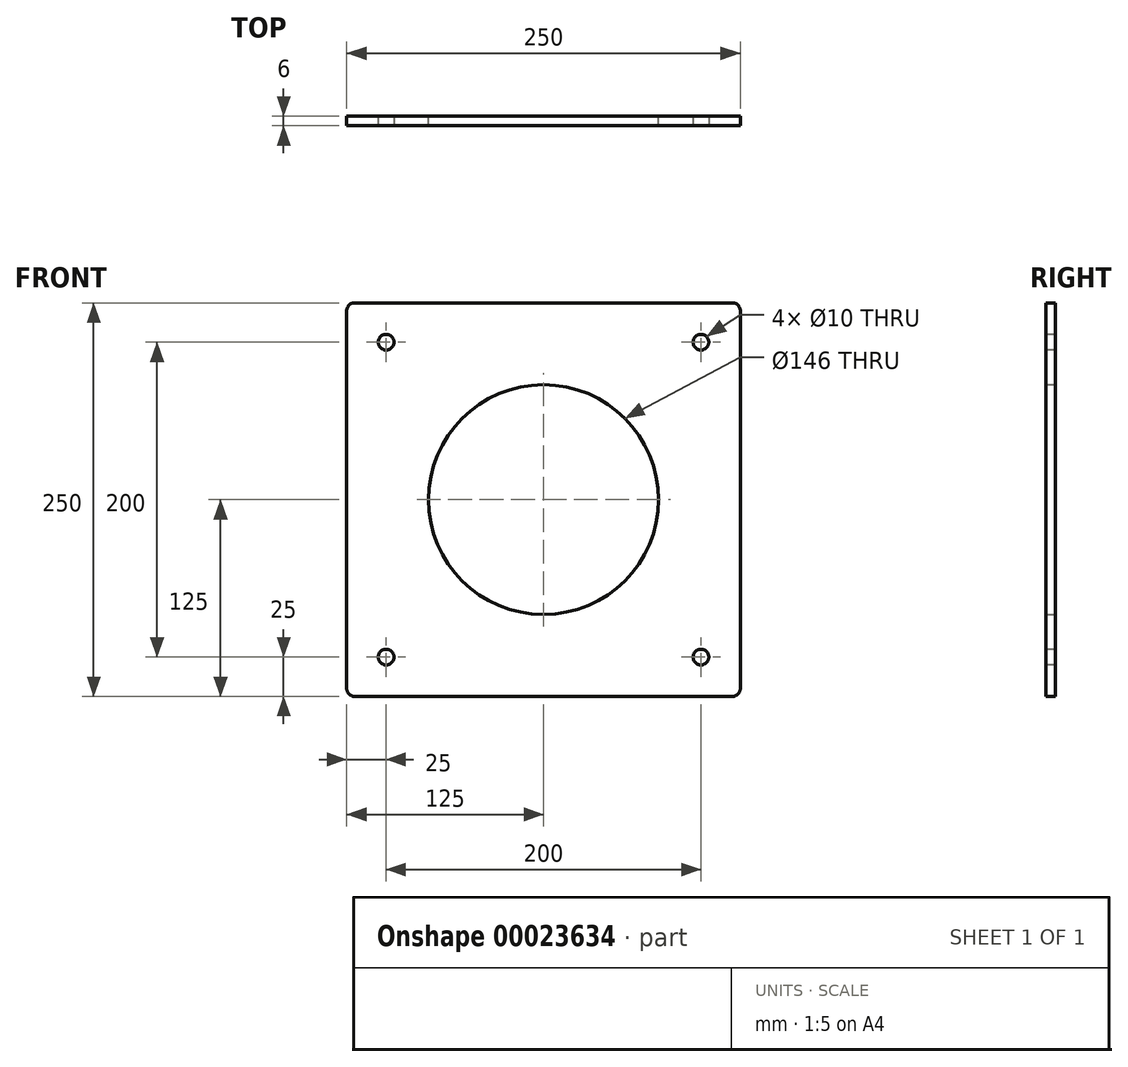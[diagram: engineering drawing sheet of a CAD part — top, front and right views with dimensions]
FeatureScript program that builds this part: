
annotation { "Feature Type Name" : "Feature", "Feature Type Description" : "" }
export const myFeature = defineFeature(function(context is Context, id is Id, definition is map)
    precondition{}
    {
        {
            var Q0;
            Q0=qCreatedBy(makeId("Front.planeOp"),FACE);
            var sketch = newSketch(context, id + "F0", { "sketchPlane" : qUnion([Q0])});
            skLineSegment(sketch, "E0.rect.bottom", {"start": v(120, 125) * mm, "end": v(-120, 125) * mm});
            skLineSegment(sketch, "E0.rect.top", {"start": v(120, -125) * mm, "end": v(-120, -125) * mm});
            skLineSegment(sketch, "E0.rect.left", {"start": v(125, 120) * mm, "end": v(125, -120) * mm});
            skLineSegment(sketch, "E0.rect.right", {"start": v(-125, 120) * mm, "end": v(-125, -120) * mm});
            skPoint(sketch, "E0.rect.middle", {"position": v(0, 0) * mm});
            skCircle(sketch, "E1", {"center": v(0, 0) * mm, "radius": 73 * mm});
            skPoint(sketch, "E2.visualSharp", {"position": v(-125, -125) * mm});
            skArc(sketch, "E2.filletArc", {"start": v(-125, -120) * mm, "mid": v(-123.54, -123.54) * mm, "end": v(-120, -125) * mm});
            skPoint(sketch, "E3.visualSharp", {"position": v(-125, 125) * mm});
            skArc(sketch, "E3.filletArc", {"start": v(-120, 125) * mm, "mid": v(-123.54, 123.54) * mm, "end": v(-125, 120) * mm});
            skPoint(sketch, "E4.visualSharp", {"position": v(125, 125) * mm});
            skArc(sketch, "E4.filletArc", {"start": v(125, 120) * mm, "mid": v(123.54, 123.54) * mm, "end": v(120, 125) * mm});
            skPoint(sketch, "E5.visualSharp", {"position": v(125, -125) * mm});
            skArc(sketch, "E5.filletArc", {"start": v(120, -125) * mm, "mid": v(123.54, -123.54) * mm, "end": v(125, -120) * mm});
            skSolve(sketch);
        }
        {
            var Q0;
            Q0 = qSketchRegion(id + "F0", true);
            extrude(context, id + "F1", {"entities" : qUnion([Q0]), "depth" : 6 * mm});
        }
        {
            var Q0;
            Q0=makeQuery(id+"F1.opExtrude","CAP_FACE",FACE,{"disambiguationData":[OSD([sQuery(id+"F0.wireOp",EDGE,"E0.rect.bottom"),sQuery(id+"F0.wireOp",EDGE,"E0.rect.top"),sQuery(id+"F0.wireOp",EDGE,"E0.rect.left"),sQuery(id+"F0.wireOp",EDGE,"E0.rect.right"),sQuery(id+"F0.wireOp",EDGE,"E1")])],"isStart":false});
            var sketch = newSketch(context, id + "F2", { "sketchPlane" : qUnion([Q0])});
            skCircle(sketch, "E6", {"center": v(-100, 100) * mm, "radius": 5 * mm});
            skLineSegment(sketch, "E7", {"start": v(0, 125) * mm, "end": v(0, -125) * mm, "construction": true});
            skLineSegment(sketch, "E8", {"start": v(-125, 0) * mm, "end": v(125, 0) * mm, "construction": true});
            skLineSegment(sketch, "E9.MirrorCS", {"start": v(125, 0) * mm, "end": v(-125, 0) * mm});
            skCircle(sketch, "E10.MirrorC", {"center": v(100, 100) * mm, "radius": 5 * mm});
            skCircle(sketch, "E11.MirrorC", {"center": v(100, -100) * mm, "radius": 5 * mm});
            skCircle(sketch, "E12.MirrorC", {"center": v(-100, -100) * mm, "radius": 5 * mm});
            skSolve(sketch);
        }
        {
            var Q0;
            Q0 = qSketchRegion(id + "F2", true);
            extrude(context, id + "F3", {"entities" : qUnion([Q0]), "operationType" : NewBodyOperationType.REMOVE, "endBound" : BoundingType.THROUGH_ALL, "oppositeDirection" : true, "depth" : 25 * mm});
        }
    });
